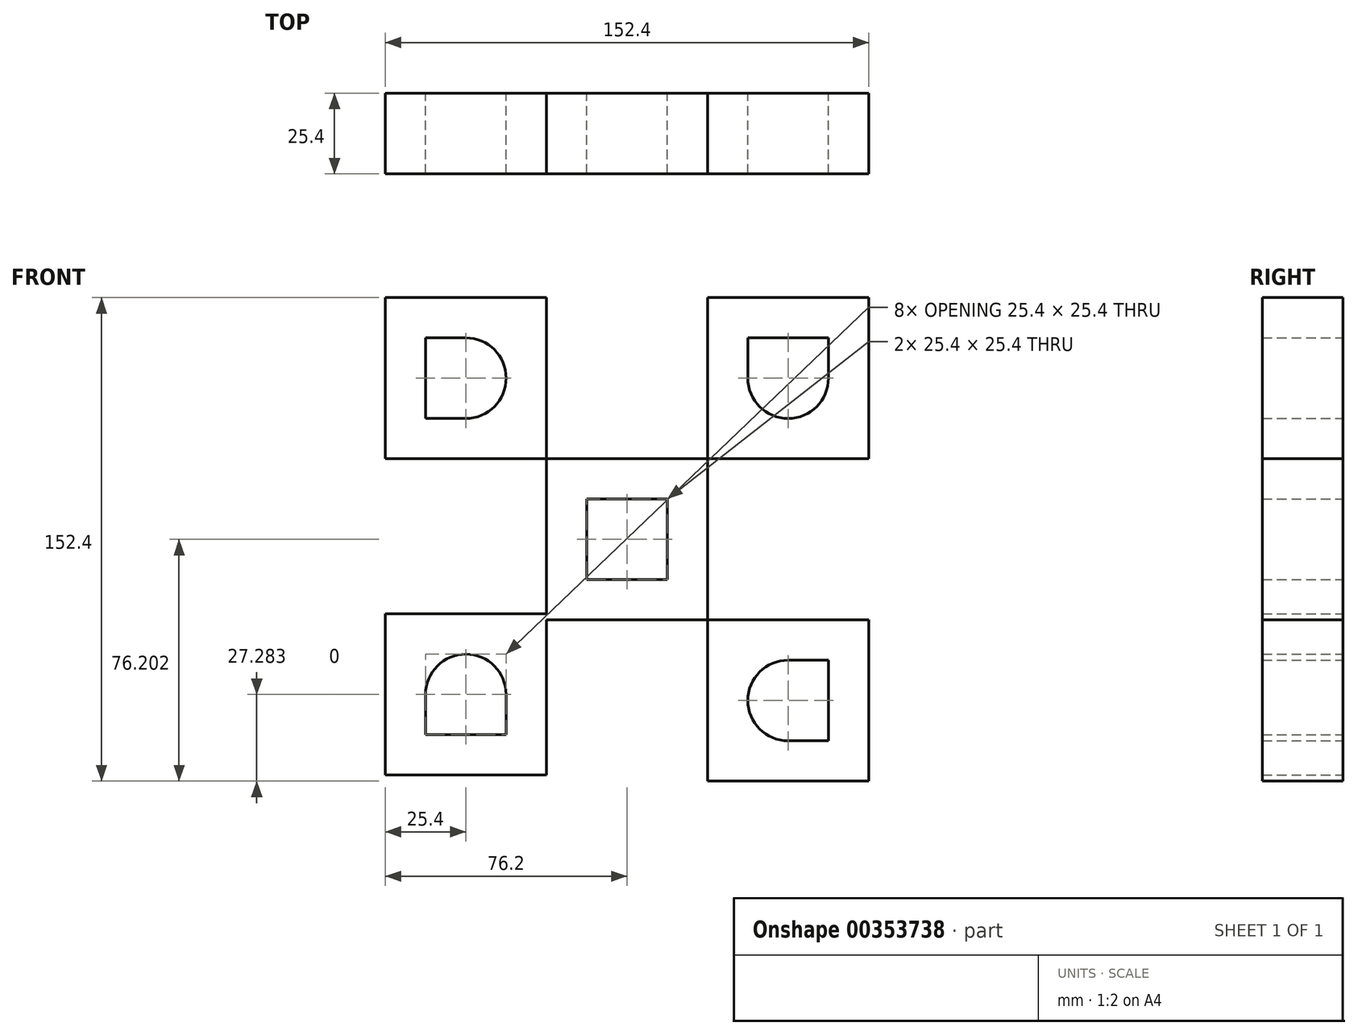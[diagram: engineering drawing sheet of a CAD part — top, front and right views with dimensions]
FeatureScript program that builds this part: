
annotation { "Feature Type Name" : "Feature", "Feature Type Description" : "" }
export const myFeature = defineFeature(function(context is Context, id is Id, definition is map)
    precondition{}
    {
        {
            var Q0;
            Q0=qCreatedBy(makeId("Front.planeOp"),FACE);
            var sketch = newSketch(context, id + "F0", { "sketchPlane" : qUnion([Q0])});
            skLineSegment(sketch, "E0.bottom", {"start": v(-50.8, 2.8) * mm, "end": v(0, 2.8) * mm});
            skLineSegment(sketch, "E0.top", {"start": v(-50.8, 53.6) * mm, "end": v(0, 53.6) * mm});
            skLineSegment(sketch, "E0.left", {"start": v(-50.8, 2.8) * mm, "end": v(-50.8, 53.6) * mm});
            skLineSegment(sketch, "E0.right", {"start": v(0, 2.8) * mm, "end": v(0, 53.6) * mm});
            skLineSegment(sketch, "E1.bottom", {"start": v(-50.8, -48) * mm, "end": v(0, -48) * mm});
            skLineSegment(sketch, "E1.top", {"start": v(-50.8, -98.8) * mm, "end": v(0, -98.8) * mm});
            skLineSegment(sketch, "E1.left", {"start": v(-50.8, -48) * mm, "end": v(-50.8, -98.8) * mm});
            skLineSegment(sketch, "E1.right", {"start": v(0, -48) * mm, "end": v(0, -98.8) * mm});
            skLineSegment(sketch, "E2.bottom", {"start": v(-101.6, 2.8) * mm, "end": v(-152.4, 2.8) * mm});
            skLineSegment(sketch, "E2.top", {"start": v(-101.6, 53.6) * mm, "end": v(-152.4, 53.6) * mm});
            skLineSegment(sketch, "E2.left", {"start": v(-101.6, 2.8) * mm, "end": v(-101.6, 53.6) * mm});
            skLineSegment(sketch, "E2.right", {"start": v(-152.4, 2.8) * mm, "end": v(-152.4, 53.6) * mm});
            skLineSegment(sketch, "E3.bottom", {"start": v(-101.6, -46.12) * mm, "end": v(-152.4, -46.12) * mm});
            skLineSegment(sketch, "E3.top", {"start": v(-101.6, -96.92) * mm, "end": v(-152.4, -96.92) * mm});
            skLineSegment(sketch, "E3.left", {"start": v(-101.6, -46.12) * mm, "end": v(-101.6, -96.92) * mm});
            skLineSegment(sketch, "E3.right", {"start": v(-152.4, -46.12) * mm, "end": v(-152.4, -96.92) * mm});
            skLineSegment(sketch, "E4.bottom", {"start": v(-101.6, 2.8) * mm, "end": v(-50.8, 2.8) * mm});
            skLineSegment(sketch, "E4.top", {"start": v(-101.6, -48) * mm, "end": v(-50.8, -48) * mm});
            skLineSegment(sketch, "E4.left", {"start": v(-101.6, 2.8) * mm, "end": v(-101.6, -48) * mm});
            skLineSegment(sketch, "E4.right", {"start": v(-50.8, 2.8) * mm, "end": v(-50.8, -48) * mm});
            skLineSegment(sketch, "E5.bottom", {"start": v(-63.5, -9.9) * mm, "end": v(-88.9, -9.9) * mm});
            skLineSegment(sketch, "E5.top", {"start": v(-63.5, -35.3) * mm, "end": v(-88.9, -35.3) * mm});
            skLineSegment(sketch, "E5.left", {"start": v(-63.5, -9.9) * mm, "end": v(-63.5, -35.3) * mm});
            skLineSegment(sketch, "E5.right", {"start": v(-88.9, -9.9) * mm, "end": v(-88.9, -35.3) * mm});
            skPoint(sketch, "E5.middle", {"position": v(-76.2, -22.6) * mm});
            skPoint(sketch, "E5.middle.positionSnap0", {"position": v(-50.8, -22.6) * mm});
            skPoint(sketch, "E5.middle.positionSnap1", {"position": v(-76.2, 2.8) * mm});
            skPoint(sketch, "E5.centerSnap0", {"position": v(-50.8, -22.6) * mm});
            skPoint(sketch, "E5.centerSnap1", {"position": v(-76.2, 2.8) * mm});
            skLineSegment(sketch, "E6.bottom", {"start": v(-12.7, 40.9) * mm, "end": v(-38.1, 40.9) * mm});
            skLineSegment(sketch, "E6.left", {"start": v(-12.7, 40.9) * mm, "end": v(-12.7, 28.2) * mm});
            skLineSegment(sketch, "E6.right", {"start": v(-38.1, 40.9) * mm, "end": v(-38.1, 28.2) * mm});
            skPoint(sketch, "E6.middle", {"position": v(-25.4, 28.2) * mm});
            skPoint(sketch, "E6.middle.positionSnap0", {"position": v(0, 28.2) * mm});
            skPoint(sketch, "E6.middle.positionSnap1", {"position": v(-25.4, 53.6) * mm});
            skPoint(sketch, "E6.centerSnap0", {"position": v(0, 28.2) * mm});
            skPoint(sketch, "E6.centerSnap1", {"position": v(-25.4, 53.6) * mm});
            skLineSegment(sketch, "E7.bottom", {"start": v(-127, 40.9) * mm, "end": v(-139.7, 40.9) * mm});
            skLineSegment(sketch, "E7.top", {"start": v(-127, 15.5) * mm, "end": v(-139.7, 15.5) * mm});
            skLineSegment(sketch, "E7.right", {"start": v(-139.7, 40.9) * mm, "end": v(-139.7, 15.5) * mm});
            skPoint(sketch, "E7.middle", {"position": v(-127, 28.2) * mm});
            skPoint(sketch, "E7.middle.positionSnap0", {"position": v(-101.6, 28.2) * mm});
            skPoint(sketch, "E7.middle.positionSnap1", {"position": v(-127, 53.6) * mm});
            skPoint(sketch, "E7.centerSnap0", {"position": v(-101.6, 28.2) * mm});
            skPoint(sketch, "E7.centerSnap1", {"position": v(-127, 53.6) * mm});
            skLineSegment(sketch, "E8.top", {"start": v(-114.3, -84.22) * mm, "end": v(-139.7, -84.22) * mm});
            skLineSegment(sketch, "E8.left", {"start": v(-114.3, -71.52) * mm, "end": v(-114.3, -84.22) * mm});
            skLineSegment(sketch, "E8.right", {"start": v(-139.7, -71.52) * mm, "end": v(-139.7, -84.22) * mm});
            skPoint(sketch, "E8.middle", {"position": v(-127, -71.52) * mm});
            skPoint(sketch, "E8.middle.positionSnap0", {"position": v(-101.6, -71.52) * mm});
            skPoint(sketch, "E8.middle.positionSnap1", {"position": v(-127, -46.12) * mm});
            skPoint(sketch, "E8.centerSnap0", {"position": v(-101.6, -71.52) * mm});
            skPoint(sketch, "E8.centerSnap1", {"position": v(-127, -46.12) * mm});
            skLineSegment(sketch, "E9.bottom", {"start": v(-12.7, -60.7) * mm, "end": v(-25.4, -60.7) * mm});
            skLineSegment(sketch, "E9.top", {"start": v(-12.7, -86.1) * mm, "end": v(-25.4, -86.1) * mm});
            skLineSegment(sketch, "E9.left", {"start": v(-12.7, -60.7) * mm, "end": v(-12.7, -86.1) * mm});
            skPoint(sketch, "E9.middle", {"position": v(-25.4, -73.4) * mm});
            skPoint(sketch, "E9.middle.positionSnap0", {"position": v(-25.4, -48) * mm});
            skPoint(sketch, "E9.middle.positionSnap1", {"position": v(-50.8, -73.4) * mm});
            skPoint(sketch, "E9.centerSnap0", {"position": v(-25.4, -48) * mm});
            skPoint(sketch, "E9.centerSnap1", {"position": v(-50.8, -73.4) * mm});
            skCircle(sketch, "E10", {"center": v(-25.4, 28.2) * mm, "radius": 12.7 * mm});
            skCircle(sketch, "E11", {"center": v(-25.4, -73.4) * mm, "radius": 12.7 * mm});
            skCircle(sketch, "E12", {"center": v(-127, -71.52) * mm, "radius": 12.7 * mm});
            skCircle(sketch, "E13", {"center": v(-127, 28.2) * mm, "radius": 12.7 * mm});
            skPoint(sketch, "E14.orphan", {"position": v(-12.7, 15.5) * mm});
            skPoint(sketch, "E6.top.end.orphan", {"position": v(-38.1, 15.5) * mm});
            skPoint(sketch, "E15.orphan", {"position": v(-38.1, -60.7) * mm});
            skPoint(sketch, "E16.orphan", {"position": v(-38.1, -86.1) * mm});
            skPoint(sketch, "E17.orphan", {"position": v(-139.7, -58.82) * mm});
            skPoint(sketch, "E18.orphan", {"position": v(-114.3, -58.82) * mm});
            skPoint(sketch, "E19.orphan", {"position": v(-114.3, 15.5) * mm});
            skPoint(sketch, "E7.left.start.orphan", {"position": v(-114.3, 40.9) * mm});
            skSolve(sketch);
        }
        {
            var Q0;
            Q0=makeQuery(id+"F0.imprint","IMPRINT",FACE,{"disambiguationData":[TD([[makeQuery(id+"F0.imprint","IMPRINT",EDGE,{"derivedFrom":sQuery(id+"F0.wireOp",EDGE,"E0.bottom")}),1.0]])]});
            var Q1;
            Q1=makeQuery(id+"F0.imprint","IMPRINT",FACE,{"disambiguationData":[TD([[makeQuery(id+"F0.imprint","IMPRINT",EDGE,{"derivedFrom":sQuery(id+"F0.wireOp",EDGE,"E1.bottom")}),-1.0]])]});
            var Q2;
            Q2=makeQuery(id+"F0.imprint","IMPRINT",FACE,{"disambiguationData":[TD([[makeQuery(id+"F0.imprint","IMPRINT",EDGE,{"derivedFrom":sQuery(id+"F0.wireOp",EDGE,"E2.bottom")}),-1.0]])]});
            var Q3;
            {var subQ1=sQuery(id+"F0.wireOp",EDGE,"E3.bottom");Q3=makeQuery(id+"F0.imprint","IMPRINT",FACE,{"disambiguationData":[TD([[makeQuery(id+"F0.imprint","IMPRINT",EDGE,{"derivedFrom":subQ1}),1.0]])]});}
            var Q4;
            {var subQ3=sQuery(id+"F0.wireOp",EDGE,"E4.bottom");Q4=makeQuery(id+"F0.imprint","IMPRINT",FACE,{"disambiguationData":[TD([[makeQuery(id+"F0.imprint","IMPRINT",EDGE,{"derivedFrom":subQ3}),-1.0]])]});}
            extrude(context, id + "F1", {"entities" : qUnion([Q0, Q1, Q2, Q3, Q4]), "depth" : 25.4 * mm});
        }
        {
            var Q0;
            Q0 = qSketchRegion(id + "F0", true);
            extrude(context, id + "F2", {"entities" : qUnion([Q0]), "depth" : 25.4 * mm});
        }
    });
